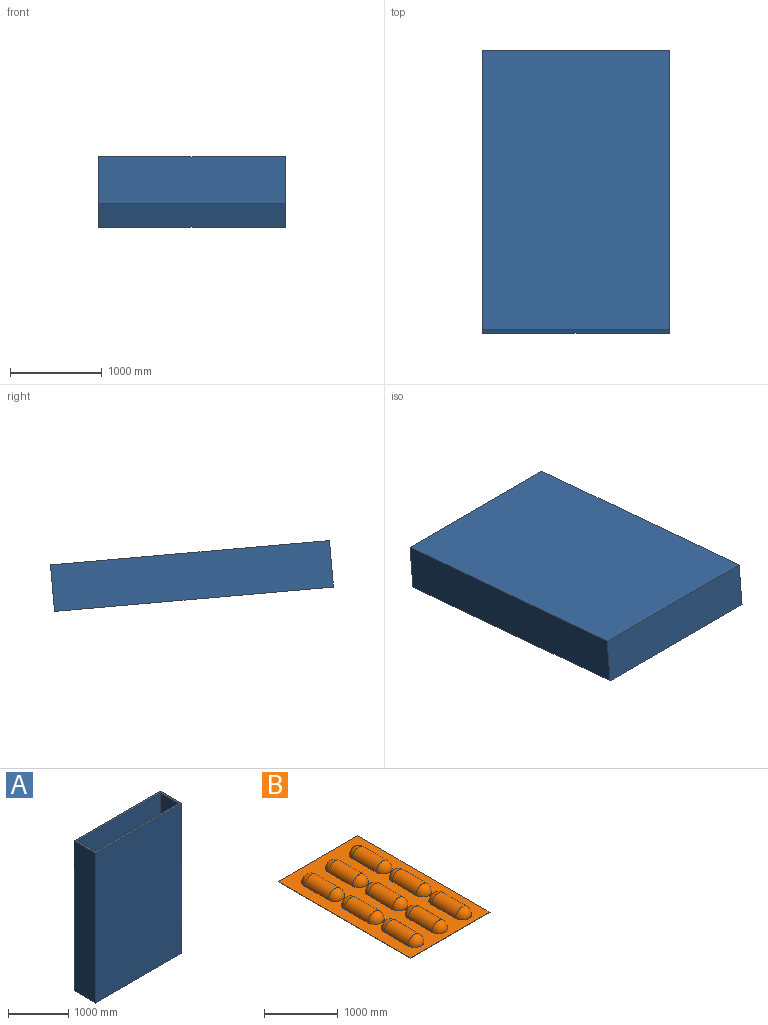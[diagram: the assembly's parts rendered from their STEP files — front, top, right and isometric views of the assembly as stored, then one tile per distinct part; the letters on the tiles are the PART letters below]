
ASSEMBLY  parts=2 mates=1
PART A: 11 faces, bbox 2032x508x3048 mm
  f0: plane 2032x508mm, normal (0,0,1), area 187741.6mm2, adj f1,f3,f4,f5,f6,f7,f8,f9
  f1: plane 3048x508mm, normal (-1,0,0), area 1548384mm2, adj f0,f2,f4,f5
  f2: plane 2032x508mm, normal (0,0,-1), area 1032256mm2, adj f1,f3,f4,f5
  f3: plane 3048x508mm, normal (1,0,0), area 1548384mm2, adj f0,f2,f4,f5
  f4: plane 3048x2032mm, normal (0,1,0), area 6193536mm2, adj f0,f1,f2,f3
  f5: plane 3048x2032mm, normal (0,-1,0), area 6193536mm2, adj f0,f1,f2,f3
  f6: plane 3009.9x431.8mm, normal (-1,0,0), area 1299674.8mm2, adj f0,f7,f9,f10
  f7: plane 3009.9x1955.8mm, normal (0,-1,0), area 5886762.4mm2, adj f0,f6,f8,f10
  f8: plane 3009.9x431.8mm, normal (1,0,0), area 1299674.8mm2, adj f0,f7,f9,f10
  f9: plane 3009.9x1955.8mm, normal (0,1,0), area 5886762.4mm2, adj f0,f6,f8,f10
  f10: plane 1955.8x431.8mm, normal (0,0,1), area 844514.4mm2, adj f6,f7,f8,f9
PART B: 33 faces, bbox 1524x2540x131.6 mm
  f0: plane 1524x4.57mm, normal (0,1,0), area 6967.7mm2, adj f1,f3,f4,f5
  f1: plane 2540x4.57mm, normal (-1,0,0), area 11612.9mm2, adj f0,f2,f4,f5
  f2: plane 1524x4.57mm, normal (0,-1,0), area 6967.7mm2, adj f1,f3,f4,f5
  f3: plane 2540x4.57mm, normal (1,0,0), area 11612.9mm2, adj f0,f2,f4,f5
  f4: plane 2540x1524mm, normal (0,0,1), area 2369764.1mm2, adj f0,f1,f2,f3,f6,f7,f8,f9
  f5: plane 2540x1524mm, normal (0,0,-1), area 3870960mm2, adj f0,f1,f2,f3
  f6: sphere r=127mm, area 50670.7mm2, adj f4,f7
  f7: cylinder r=127mm len=457.2mm, axis (0,-1,0), area 182414.7mm2, adj f4,f6,f8
  f8: sphere r=127mm, area 50670.7mm2, adj f4,f7
  f9: sphere r=127mm, area 50670.7mm2, adj f4,f10
  f10: cylinder r=127mm len=457.2mm, axis (0,-1,0), area 182414.7mm2, adj f4,f9,f11
  f11: sphere r=127mm, area 50670.7mm2, adj f4,f10
  f12: sphere r=127mm, area 50670.7mm2, adj f4,f13
  f13: cylinder r=127mm len=457.2mm, axis (0,-1,0), area 182414.7mm2, adj f4,f12,f14
  f14: sphere r=127mm, area 50670.7mm2, adj f4,f13
  f15: sphere r=127mm, area 50670.7mm2, adj f4,f16
  f16: cylinder r=127mm len=457.2mm, axis (0,-1,0), area 182414.7mm2, adj f4,f15,f17
  f17: sphere r=127mm, area 50670.7mm2, adj f4,f16
  f18: sphere r=127mm, area 50670.7mm2, adj f4,f19
  f19: cylinder r=127mm len=457.2mm, axis (0,-1,0), area 182414.7mm2, adj f4,f18,f20
  f20: sphere r=127mm, area 50670.7mm2, adj f4,f19
  f21: sphere r=127mm, area 50670.7mm2, adj f4,f22
  f22: cylinder r=127mm len=457.2mm, axis (0,-1,0), area 182414.7mm2, adj f4,f21,f23
  f23: sphere r=127mm, area 50670.7mm2, adj f4,f22
  f24: sphere r=127mm, area 50670.7mm2, adj f4,f25
  f25: cylinder r=127mm len=457.2mm, axis (0,-1,0), area 182414.7mm2, adj f4,f24,f26
  f26: sphere r=127mm, area 50670.7mm2, adj f4,f25
  f27: sphere r=127mm, area 50670.7mm2, adj f4,f28
  f28: cylinder r=127mm len=457.2mm, axis (0,-1,0), area 182414.7mm2, adj f4,f27,f29
  f29: sphere r=127mm, area 50670.7mm2, adj f4,f28
  f30: sphere r=127mm, area 50670.7mm2, adj f4,f31
  f31: cylinder r=127mm len=457.2mm, axis (0,-1,0), area 182414.7mm2, adj f4,f30,f32
  f32: sphere r=127mm, area 50670.7mm2, adj f4,f31
PLACE A rot(axis=(-1,0,0),95deg) t=(-1751.67,-2290.79,2705.39)mm
PLACE B rot(axis=(-1,0,0),5deg) t=(-1528.09,-1876.49,2197.45)mm
MATE planar A.f7 <-> B.f5  axis (0,0.09,1) through (242.23,-794.57,2102.8)mm
